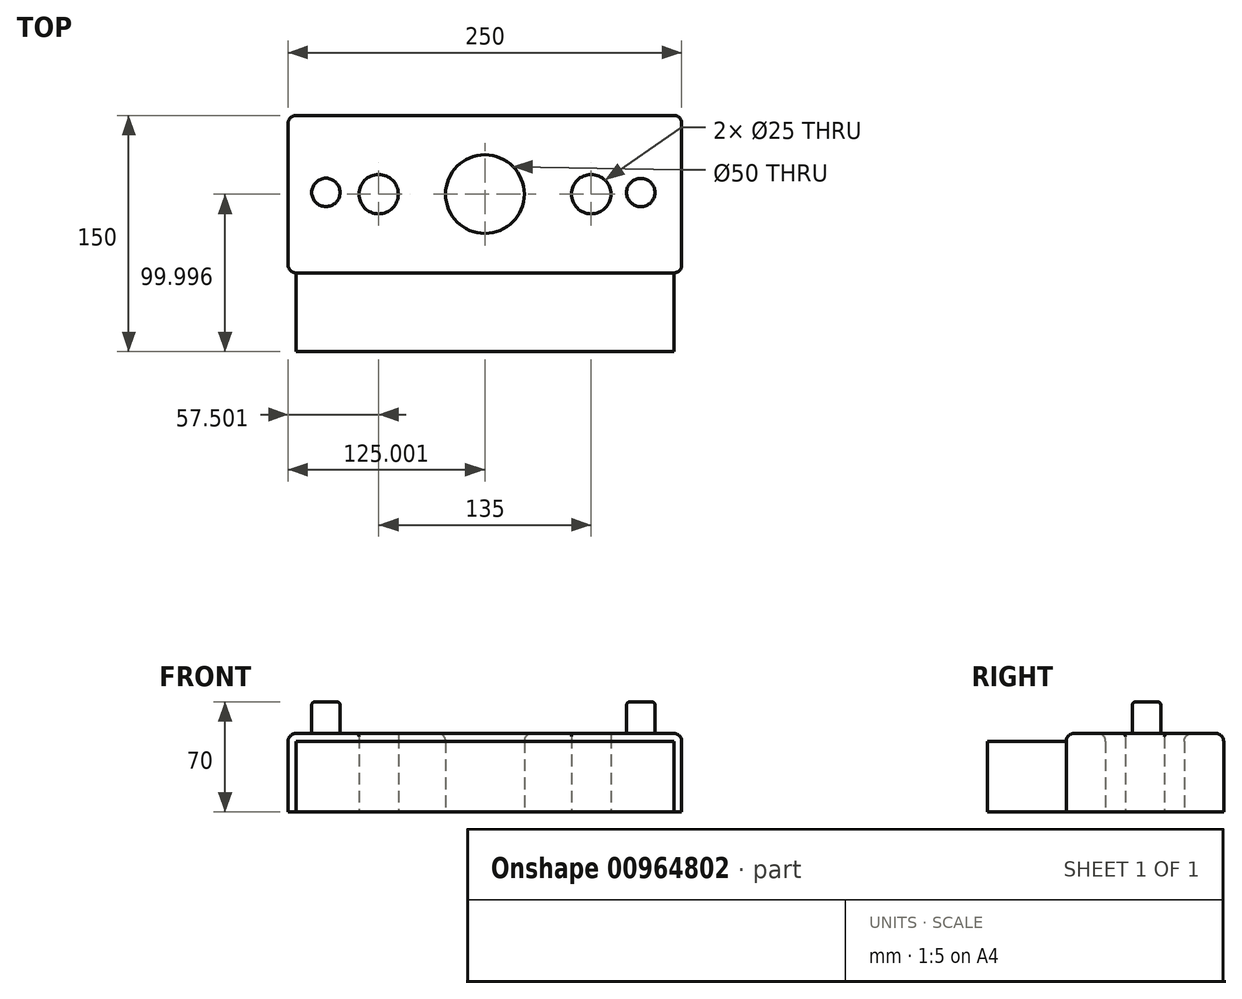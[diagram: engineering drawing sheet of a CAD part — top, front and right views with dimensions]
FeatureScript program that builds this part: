
annotation { "Feature Type Name" : "Feature", "Feature Type Description" : "" }
export const myFeature = defineFeature(function(context is Context, id is Id, definition is map)
    precondition{}
    {
        {
            var Q0;
            Q0=qCreatedBy(makeId("Top.planeOp"),FACE);
            var sketch = newSketch(context, id + "F0", { "sketchPlane" : qUnion([Q0])});
            skLineSegment(sketch, "E0.bottom", {"start": v(-211.65, 82.36) * mm, "end": v(38.35, 82.36) * mm});
            skLineSegment(sketch, "E0.top", {"start": v(-211.65, -17.64) * mm, "end": v(38.35, -17.64) * mm});
            skLineSegment(sketch, "E0.left", {"start": v(-211.65, 82.36) * mm, "end": v(-211.65, -17.64) * mm});
            skLineSegment(sketch, "E0.right", {"start": v(38.35, 82.36) * mm, "end": v(38.35, -17.64) * mm});
            skCircle(sketch, "E1", {"center": v(-86.65, 32.36) * mm, "radius": 25 * mm});
            skPoint(sketch, "E1.centerSnap0", {"position": v(-86.65, -17.64) * mm});
            skPoint(sketch, "E1.centerSnap1", {"position": v(38.35, 32.36) * mm});
            skCircle(sketch, "E2", {"center": v(-154.15, 32.36) * mm, "radius": 12.5 * mm});
            skCircle(sketch, "E3", {"center": v(-19.15, 32.36) * mm, "radius": 12.5 * mm});
            skSolve(sketch);
        }
        {
            var Q0;
            Q0=makeQuery(id+"F0.imprint","IMPRINT",FACE,{"disambiguationData":[TD([[makeQuery(id+"F0.imprint","IMPRINT",EDGE,{"derivedFrom":sQuery(id+"F0.wireOp",EDGE,"E0.bottom")}),-1.0]])]});
            extrude(context, id + "F1", {"entities" : qUnion([Q0]), "depth" : 50 * mm, "offsetDistance" : 25 * mm});
        }
        {
            var Q0;
            Q0=makeQuery(id+"F1.opExtrude","CAP_EDGE",EDGE,{"disambiguationData":[OSD([sQuery(id+"F0.wireOp",EDGE,"E1")])],"isStart":false});
            fillet(context, id + "F2", {"entities" : qUnion([Q0]), "radius" : 5 * mm, "tangentPropagation" : true, "allowEdgeOverflow" : false});
        }
        {
            var Q0;
            Q0=makeQuery(id+"F1.opExtrude","CAP_EDGE",EDGE,{"disambiguationData":[OSD([sQuery(id+"F0.wireOp",EDGE,"E0.top")])],"isStart":false});
            var Q1;
            Q1=makeQuery(id+"F1.opExtrude","CAP_EDGE",EDGE,{"disambiguationData":[OSD([sQuery(id+"F0.wireOp",EDGE,"E0.left")])],"isStart":false});
            var Q2;
            Q2=makeQuery(id+"F1.opExtrude","CAP_EDGE",EDGE,{"disambiguationData":[OSD([sQuery(id+"F0.wireOp",EDGE,"E0.bottom")])],"isStart":false});
            var Q3;
            Q3=makeQuery(id+"F1.opExtrude","CAP_EDGE",EDGE,{"disambiguationData":[OSD([sQuery(id+"F0.wireOp",EDGE,"E0.right")])],"isStart":false});
            var Q4;
            Q4=makeQuery(id+"F1.opExtrude","SWEPT_EDGE",EDGE,{"disambiguationData":[OSD([sQuery(id+"F0.wireOp",EDGE,"E0.top"),sQuery(id+"F0.wireOp",EDGE,"E0.right")])]});
            var Q5;
            Q5=makeQuery(id+"F1.opExtrude","SWEPT_EDGE",EDGE,{"disambiguationData":[OSD([sQuery(id+"F0.wireOp",EDGE,"E0.bottom"),sQuery(id+"F0.wireOp",EDGE,"E0.right")])]});
            var Q6;
            Q6=makeQuery(id+"F1.opExtrude","SWEPT_EDGE",EDGE,{"disambiguationData":[OSD([sQuery(id+"F0.wireOp",EDGE,"E0.top"),sQuery(id+"F0.wireOp",EDGE,"E0.left")])]});
            var Q7;
            Q7=makeQuery(id+"F1.opExtrude","SWEPT_EDGE",EDGE,{"disambiguationData":[OSD([sQuery(id+"F0.wireOp",EDGE,"E0.bottom"),sQuery(id+"F0.wireOp",EDGE,"E0.left")])]});
            fillet(context, id + "F3", {"entities" : qUnion([Q0, Q1, Q2, Q3, Q4, Q5, Q6, Q7]), "radius" : 5 * mm, "allowEdgeOverflow" : false});
        }
        {
            var Q0;
            Q0=makeQuery(id+"F1.opExtrude","CAP_FACE",FACE,{"disambiguationData":[OSD([sQuery(id+"F0.wireOp",EDGE,"E0.bottom"),sQuery(id+"F0.wireOp",EDGE,"E0.top"),sQuery(id+"F0.wireOp",EDGE,"E0.left"),sQuery(id+"F0.wireOp",EDGE,"E0.right"),sQuery(id+"F0.wireOp",EDGE,"E1"),sQuery(id+"F0.wireOp",EDGE,"E2"),sQuery(id+"F0.wireOp",EDGE,"E3")])],"isStart":false});
            var sketch = newSketch(context, id + "F4", { "sketchPlane" : qUnion([Q0])});
            skCircle(sketch, "E4", {"center": v(12.33, 33.39) * mm, "radius": 9 * mm});
            skCircle(sketch, "E5", {"center": v(-187.67, 33.47) * mm, "radius": 9 * mm});
            skSolve(sketch);
        }
        {
            var Q0;
            Q0=makeQuery(id+"F4.imprint","IMPRINT",FACE,{"disambiguationData":[TD([[makeQuery(id+"F4.imprint","IMPRINT",EDGE,{"derivedFrom":sQuery(id+"F4.wireOp",EDGE,"E5")}),1.0]])]});
            var Q1;
            Q1=makeQuery(id+"F4.imprint","IMPRINT",FACE,{"disambiguationData":[TD([[makeQuery(id+"F4.imprint","IMPRINT",EDGE,{"derivedFrom":sQuery(id+"F4.wireOp",EDGE,"E4")}),1.0]])]});
            extrude(context, id + "F5", {"entities" : qUnion([Q0, Q1]), "operationType" : NewBodyOperationType.ADD, "depth" : 20 * mm, "offsetDistance" : 25 * mm});
        }
        {
            var Q0;
            Q0=makeQuery(id+"F5.opExtrude","CAP_EDGE",EDGE,{"disambiguationData":[OSD([sQuery(id+"F4.wireOp",EDGE,"E5")])],"isStart":false});
            var Q1;
            Q1=makeQuery(id+"F5.opExtrude","CAP_EDGE",EDGE,{"disambiguationData":[OSD([sQuery(id+"F4.wireOp",EDGE,"E4")])],"isStart":false});
            var Q2;
            Q2=makeQuery(id+"F5.opExtrude","CAP_EDGE",EDGE,{"disambiguationData":[OSD([sQuery(id+"F4.wireOp",EDGE,"E4")])],"isStart":true});
            var Q3;
            Q3=makeQuery(id+"F5.opExtrude","CAP_EDGE",EDGE,{"disambiguationData":[OSD([sQuery(id+"F4.wireOp",EDGE,"E5")])],"isStart":true});
            fillet(context, id + "F6", {"entities" : qUnion([Q0, Q1, Q2, Q3]), "radius" : 2 * mm, "tangentPropagation" : true, "allowEdgeOverflow" : false});
        }
        {
            var Q0;
            Q0=makeQuery(id+"F1.opExtrude","CAP_EDGE",EDGE,{"disambiguationData":[OSD([sQuery(id+"F0.wireOp",EDGE,"E2")])],"isStart":false});
            var Q1;
            Q1=makeQuery(id+"F1.opExtrude","CAP_EDGE",EDGE,{"disambiguationData":[OSD([sQuery(id+"F0.wireOp",EDGE,"E3")])],"isStart":false});
            fillet(context, id + "F7", {"entities" : qUnion([Q0, Q1]), "radius" : 2 * mm, "tangentPropagation" : true, "allowEdgeOverflow" : false});
        }
        {
            var Q0;
            Q0=makeQuery(id+"F1.opExtrude","SWEPT_FACE",FACE,{"disambiguationData":[OSD([sQuery(id+"F0.wireOp",EDGE,"E0.top")])]});
            extrude(context, id + "F8", {"entities" : qUnion([Q0]), "operationType" : NewBodyOperationType.ADD, "depth" : 50 * mm, "offsetDistance" : 25 * mm});
        }
    });
